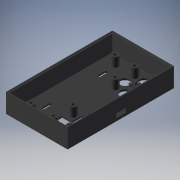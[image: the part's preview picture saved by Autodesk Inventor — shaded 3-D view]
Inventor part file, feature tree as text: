
AUTODESK INVENTOR PART (.ipt)
format: ipt  version: 2019 (Build 230136000, 136)  size: 326,144 bytes
history: native  units: mm
features: extrude x11, sketch x8
ambient origin geometry x8: Origin, YZ Plane, XZ Plane, XY Plane, X Axis, Y Axis, Z Axis, Center Point
bodies: Volumenkörper1 (feature_tree)
feature tree (19):
  extrude  "Extrusion1"  Depth=55.8mm
  extrude  "Extrusion2"  Depth=1.5mm
  sketch  "Skizze4"  dims[d5=15.75mm d6=0.0mm]
  extrude  "Extrusion3"  Depth=6.0mm
  extrude  "Extrusion4"  Depth=15.24mm
  sketch  "Skizze5"  dims[d13=4.12mm d15=4.12mm d16=4.12mm d17=6.0mm d18=6.0mm d19=6.0mm d20=6.0mm d21=2.6mm d22=2.6mm d23=2.6mm d24=2.6mm d25=17.78mm d29=17.78mm]
  extrude  "Extrusion5"  Depth=7.0mm
  extrude  "Extrusion6"  Depth=7.0mm
  extrude  "Extrusion7"  Depth=8.75mm
  extrude  "Extrusion8"  Depth=8.75mm
  extrude  "Extrusion9"  Depth=8.75mm
  extrude  "Extrusion10"  Depth=8.75mm
  extrude  "Extrusion11"  Depth=8.75mm
  sketch  "Skizze1"  dims[d0=96.44mm d1=55.8mm]
  sketch  "Skizze2"  dims[d2=1.5mm d3=0.0mm d4=1.5mm]
  sketch  "Skizze6"  dims[d30=15.24mm d31=15.24mm]
  sketch  "Skizze7"  dims[d32=4.12mm d33=7.0mm]
  sketch  "Skizze9"  dims[d34=7.0mm d35=7.0mm]
  sketch  "Skizze14"  dims[d36=7.0mm d37=8.75mm d38=8.75mm d39=8.75mm d40=8.75mm d41=8.75mm d42=8.75mm d43=8.75mm d44=8.75mm d45=5.39mm d46=8.62mm d48=5.39mm d49=15.0mm d50=0.0mm d51=8.5mm d52=0.0mm d92=9.0mm d93=9.0mm d94=9.0mm d95=9.0mm d96=8.62mm d98=8.89mm d99=8.89mm d100=8.89mm d101=8.89mm d102=6.0mm d103=2.7mm d104=6.0mm d105=2.7mm d106=6.0mm d107=2.7mm d108=6.0mm d109=2.7mm d110=8.89mm d111=15.0mm d112=0.0mm d113=8.5mm d114=0.0mm d115=2.0mm d116=1.0mm d117=1.0mm d118=1.0mm d121=1.0mm d129=1.0mm d130=1.0mm d131=1.0mm d134=5.5mm d135=5.5mm d136=5.5mm d137=5.5mm d138=2.0mm d139=2.0mm d140=2.39mm d141=2.39mm d142=2.39mm d143=1.0mm d144=2.39mm d145=3.0mm d146=0.0mm d147=6.08mm d148=6.08mm d149=6.5mm d150=2.5mm d151=19.05mm d152=1.83mm d153=6.5mm d154=2.5mm d156=16.51mm d157=1.83mm d158=3.0mm d159=0.0mm d160=6.0mm d161=6.0mm d162=2.7mm d163=2.7mm d167=0.0mm d168=0.0mm d169=17.78mm d170=20.32mm d171=8.5mm d172=0.0mm d173=4.5mm d174=1.0mm d175=8.5mm d177=44.47mm d178=8.5mm d179=0.0mm d180=0.75mm d181=0.75mm d182=0.0mm]
